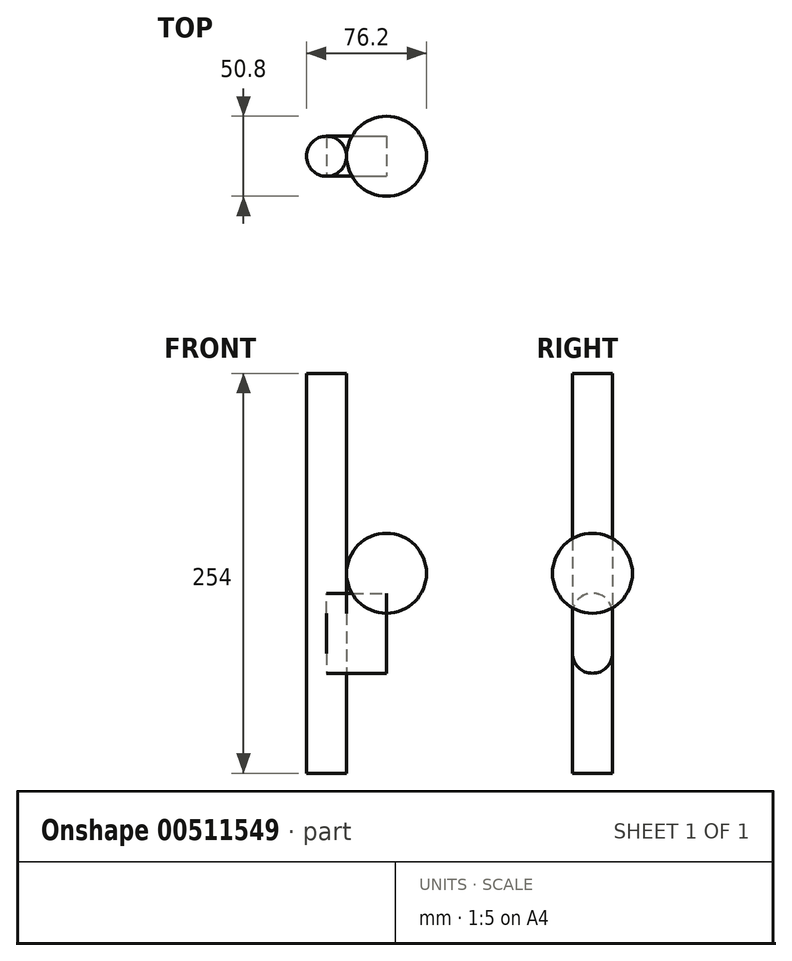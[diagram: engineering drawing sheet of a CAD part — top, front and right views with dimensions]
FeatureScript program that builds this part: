
annotation { "Feature Type Name" : "Feature", "Feature Type Description" : "" }
export const myFeature = defineFeature(function(context is Context, id is Id, definition is map)
    precondition{}
    {
        {
            var Q0;
            Q0=qCreatedBy(makeId("Top.planeOp"),FACE);
            var sketch = newSketch(context, id + "F0", { "sketchPlane" : qUnion([Q0])});
            skLineSegment(sketch, "E0", {"start": v(0, 58.87) * mm, "end": v(0, -67.38) * mm, "construction": true});
            skArc(sketch, "E1", {"start": v(0, -25.4) * mm, "mid": v(25.4, 0) * mm, "end": v(0, 25.4) * mm});
            skCircle(sketch, "E2", {"center": v(-38.1, 0) * mm, "radius": 12.7 * mm});
            skSolve(sketch);
        }
        {
            var Q0;
            Q0=sQuery(id+"F0.wireOp",EDGE,"E1");
            var Q1;
            Q1=sQuery(id+"F0.wireOp",EDGE,"E0");
            revolve(context, id + "F1", {"bodyType" : ToolBodyType.SURFACE, "surfaceEntities" : qUnion([Q0]), "axis" : qUnion([Q1]), "revolveType" : RevolveType.FULL});
        }
        {
            var Q0;
            Q0=makeQuery(id+"F0.imprint","IMPRINT",FACE,{"disambiguationData":[TD([[makeQuery(id+"F0.imprint","IMPRINT",EDGE,{"derivedFrom":sQuery(id+"F0.wireOp",EDGE,"E2")}),1.0]])]});
            extrude(context, id + "F2", {"entities" : qUnion([Q0]), "endBound" : BoundingType.SYMMETRIC, "depth" : 254 * mm});
        }
        {
            var Q0;
            Q0=qCreatedBy(makeId("Right.planeOp"),FACE);
            var sketch = newSketch(context, id + "F3", { "sketchPlane" : qUnion([Q0])});
            skCircle(sketch, "E3", {"center": v(0, -25.4) * mm, "radius": 12.7 * mm});
            skLineSegment(sketch, "E4", {"start": v(0, 50.8) * mm, "end": v(0, -50.8) * mm, "construction": true});
            skLineSegment(sketch, "E5", {"start": v(-12.7, -25.4) * mm, "end": v(-12.7, -50.8) * mm});
            skLineSegment(sketch, "E6", {"start": v(-12.7, -50.8) * mm, "end": v(12.7, -50.8) * mm});
            skLineSegment(sketch, "E7", {"start": v(12.7, -50.8) * mm, "end": v(12.7, -25.4) * mm});
            skArc(sketch, "E8", {"start": v(-12.7, -50.8) * mm, "mid": v(0, -63.5) * mm, "end": v(12.7, -50.8) * mm});
            skSolve(sketch);
        }
        {
            var Q0;
            Q0 = qSketchRegion(id + "F3", true);
            extrude(context, id + "F4", {"entities" : qUnion([Q0]), "oppositeDirection" : true, "depth" : 38.1 * mm});
        }
        {
            var Q0;
            Q0=qCreatedBy(makeId("Right.planeOp"),FACE);
            var sketch = newSketch(context, id + "F5", { "sketchPlane" : qUnion([Q0])});
            skLineSegment(sketch, "E9.0", {"start": v(0, 50.8) * mm, "end": v(0, -50.8) * mm, "construction": true});
            skArc(sketch, "E10", {"start": v(0, -38.1) * mm, "mid": v(12.7, -25.4) * mm, "end": v(0, -12.7) * mm});
            skSolve(sketch);
        }
        {
            var Q0;
            Q0=sQuery(id+"F5.wireOp",EDGE,"E10");
            var Q1;
            Q1=sQuery(id+"F5.wireOp",EDGE,"E9.0");
            revolve(context, id + "F6", {"bodyType" : ToolBodyType.SURFACE, "surfaceEntities" : qUnion([Q0]), "axis" : qUnion([Q1]), "revolveType" : RevolveType.FULL});
        }
        {
            var Q0;
            Q0=qCreatedBy(makeId("Front.planeOp"),FACE);
            var sketch = newSketch(context, id + "F7", { "sketchPlane" : qUnion([Q0])});
            skCircle(sketch, "E11", {"center": v(0, 0) * mm, "radius": 25.4 * mm});
            skLineSegment(sketch, "E12", {"start": v(-23.28, -10.16) * mm, "end": v(23.28, -10.16) * mm});
            skArc(sketch, "E13", {"start": v(-23.28, -10.16) * mm, "mid": v(0, -25.4) * mm, "end": v(23.28, -10.16) * mm});
            skLineSegment(sketch, "E14", {"start": v(0, 0) * mm, "end": v(0, -25.4) * mm, "construction": true});
            skLineSegment(sketch, "E15", {"start": v(0, -10.16) * mm, "end": v(0, -25.4) * mm});
            skLineSegment(sketch, "E16", {"start": v(23.28, -10.16) * mm, "end": v(0, -10.16) * mm});
            skLineSegment(sketch, "E17", {"start": v(0, -25.4) * mm, "end": v(0, 25.4) * mm});
            skSolve(sketch);
        }
        {
            var Q0;
            {var subQ3=sQuery(id+"F7.wireOp",EDGE,"E17");Q0=makeQuery(id+"F7.imprint","IMPRINT",FACE,{"disambiguationData":[TD([[makeQuery(id+"F7.imprint","IMPRINT",EDGE,{"derivedFrom":subQ3}),-1.0]])]});}
            var Q1;
            {var subQ3=sQuery(id+"F7.wireOp",EDGE,"E15");Q1=makeQuery(id+"F7.imprint","IMPRINT",FACE,{"disambiguationData":[TD([[makeQuery(id+"F7.imprint","IMPRINT",EDGE,{"derivedFrom":subQ3}),1.0]])]});}
            var Q2;
            Q2=sQuery(id+"F7.wireOp",EDGE,"E17");
            revolve(context, id + "F8", {"entities" : qUnion([Q0, Q1]), "axis" : qUnion([Q2]), "revolveType" : RevolveType.FULL});
        }
    });
